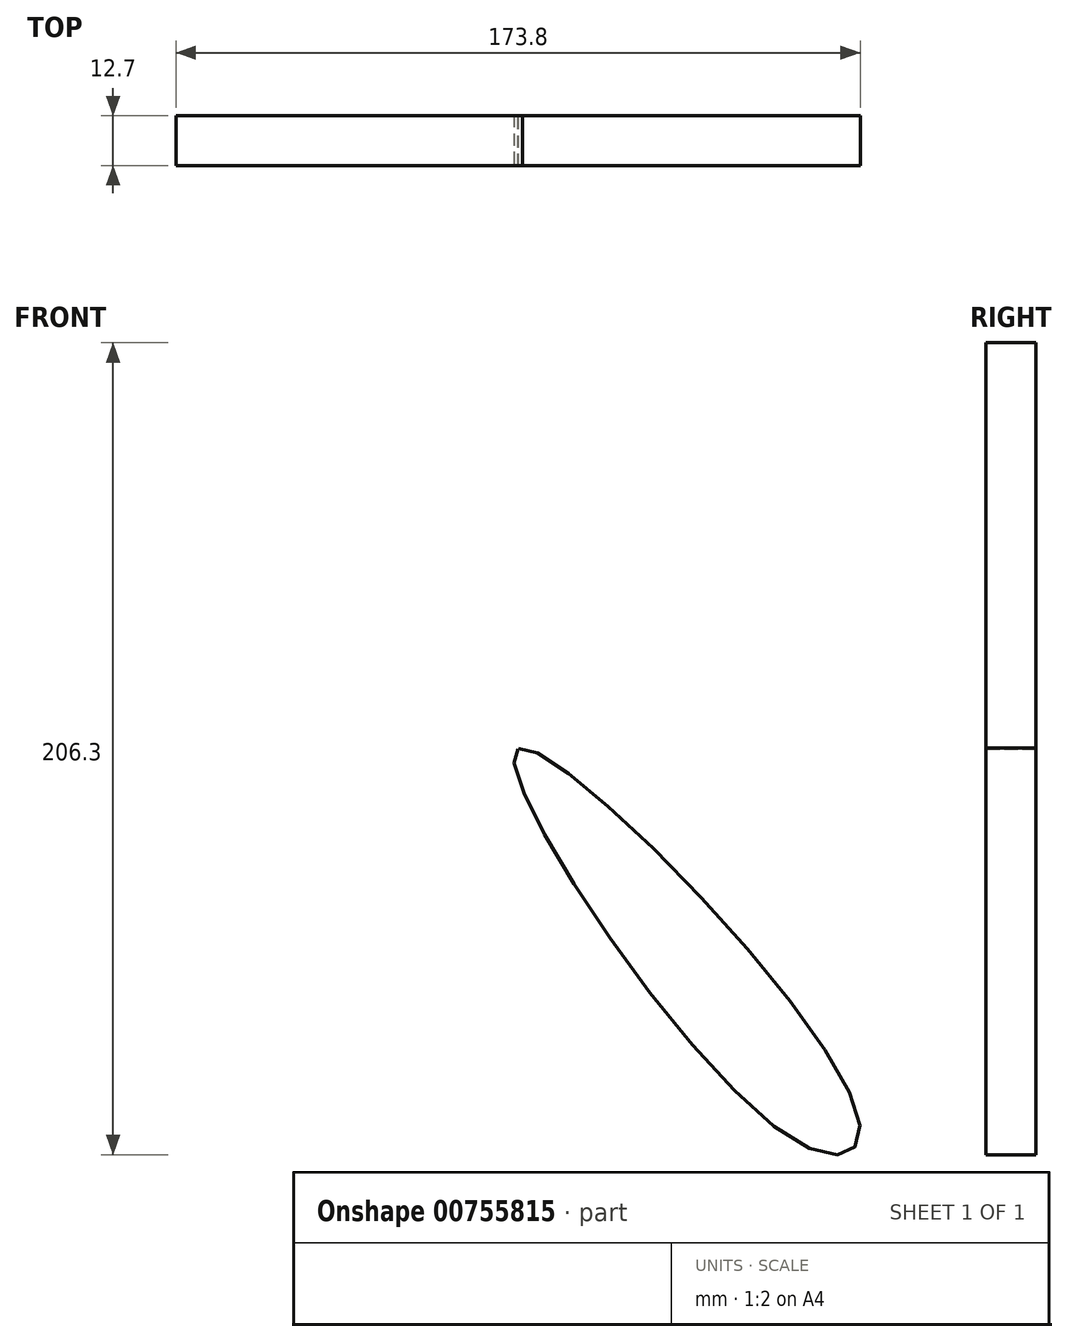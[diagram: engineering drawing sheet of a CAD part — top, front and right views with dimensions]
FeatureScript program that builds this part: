
annotation { "Feature Type Name" : "Feature", "Feature Type Description" : "" }
export const myFeature = defineFeature(function(context is Context, id is Id, definition is map)
    precondition{}
    {
        {
            var Q0;
            Q0=qCreatedBy(makeId("Front.planeOp"),FACE);
            var sketch = newSketch(context, id + "F0", { "sketchPlane" : qUnion([Q0])});
            skPoint(sketch, "E0", {"position": v(0.06, 0.02) * mm});
            skFitSpline(sketch, "E1", {"points": [v(0.06, 0.02) * mm, v(-86.65, 94.28) * mm, v(-70.95, 99.93) * mm, v(0.06, 0.02) * mm]});
            skFitSpline(sketch, "E2", {"points": [v(-0.1, -0.04) * mm, v(86.61, -94.3) * mm, v(70.9, -99.95) * mm, v(-0.1, -0.04) * mm]});
            skSolve(sketch);
        }
        {
            var Q0;
            Q0=qSketchRegion(id+"F0",true);
            extrude(context, id + "F1", {"entities" : qUnion([Q0]), "depth" : 12.7 * mm, "offsetDistance" : 25.4 * mm});
        }
    });
